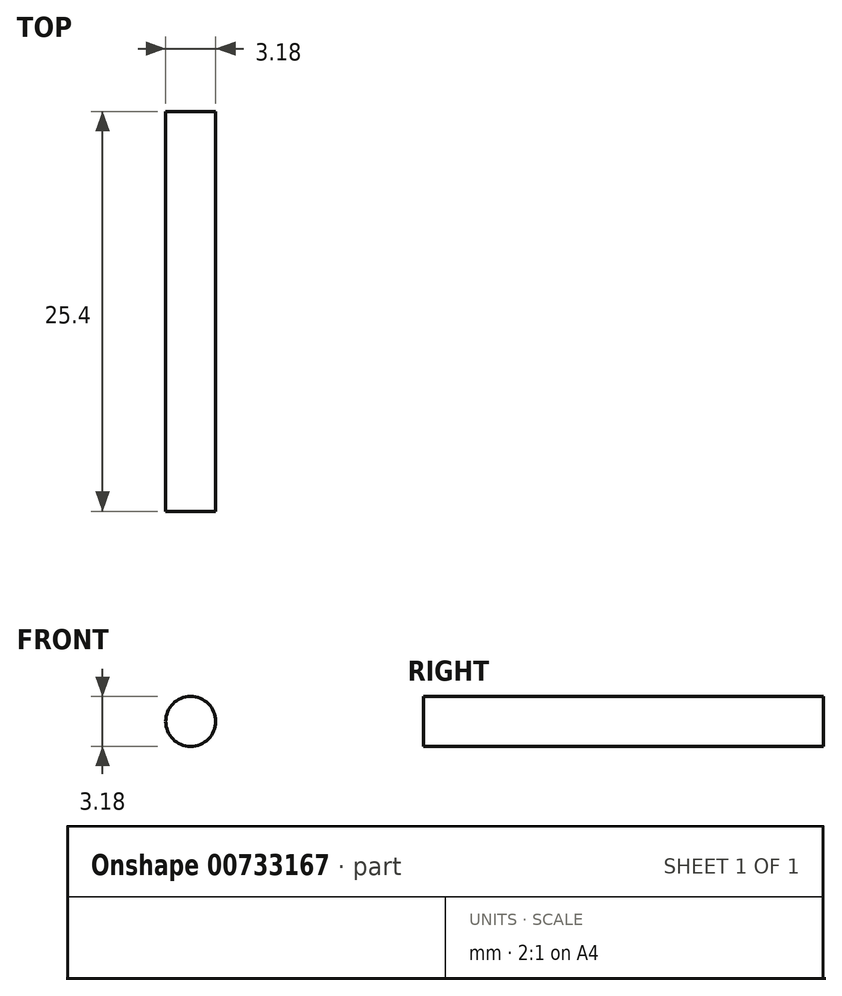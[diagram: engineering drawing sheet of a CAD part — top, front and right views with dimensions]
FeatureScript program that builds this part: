
annotation { "Feature Type Name" : "Feature", "Feature Type Description" : "" }
export const myFeature = defineFeature(function(context is Context, id is Id, definition is map)
    precondition{}
    {
        {
            var Q0;
            Q0=qCreatedBy(makeId("Front.planeOp"),FACE);
            var sketch = newSketch(context, id + "F0", { "sketchPlane" : qUnion([Q0])});
            skCircle(sketch, "E0", {"center": v(0, 0) * mm, "radius": 1.59 * mm});
            skSolve(sketch);
        }
        {
            var Q0;
            Q0 = qSketchRegion(id + "F0", true);
            extrude(context, id + "F1", {"entities" : qUnion([Q0]), "depth" : 25.4 * mm, "offsetDistance" : 25.4 * mm});
        }
    });
